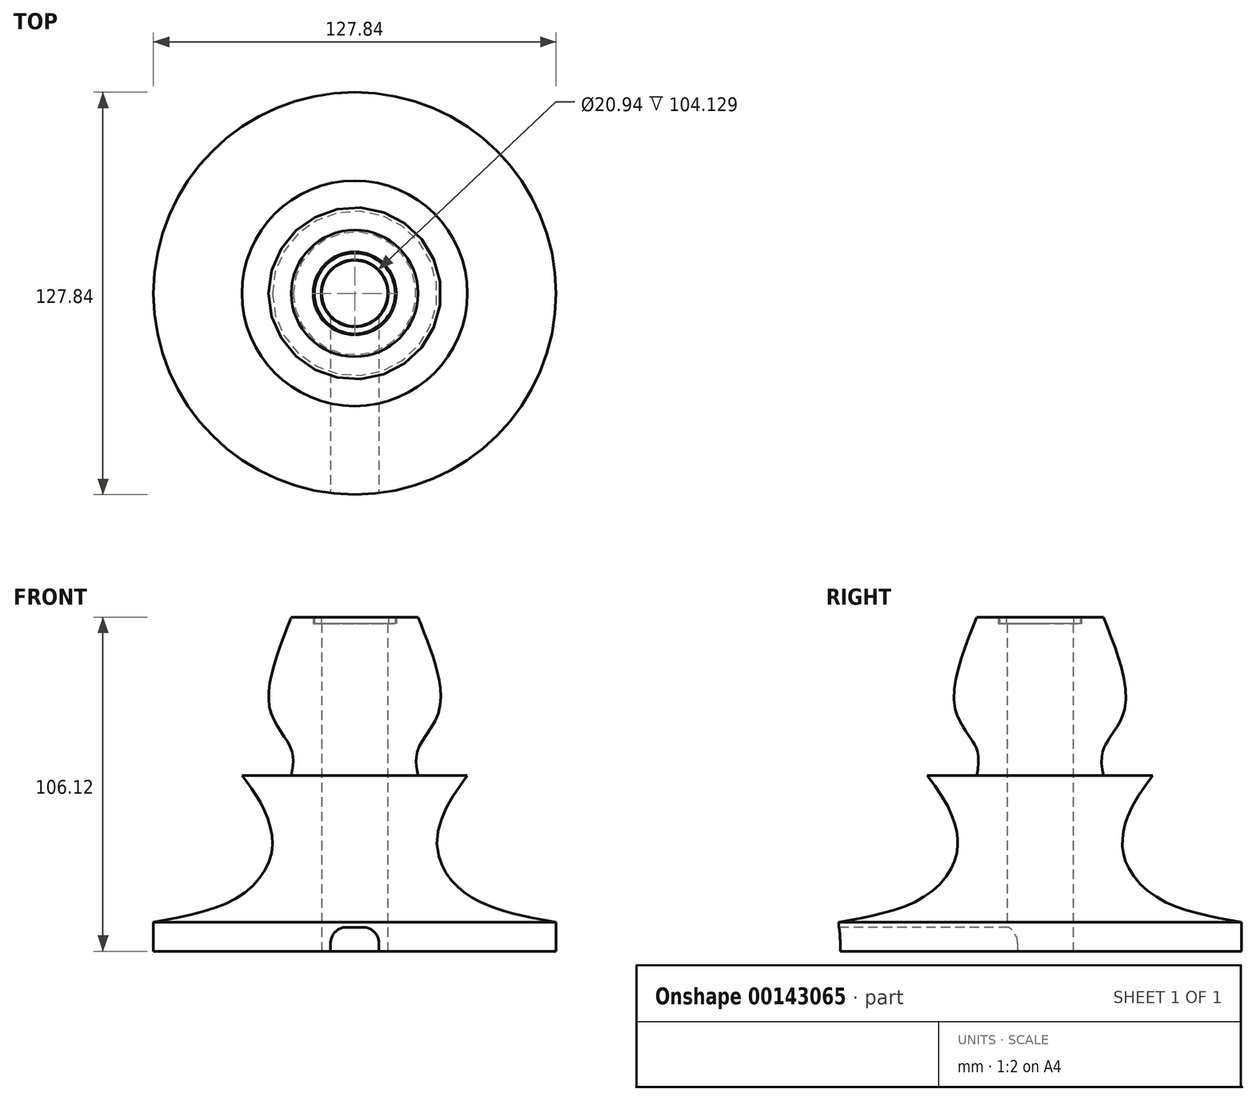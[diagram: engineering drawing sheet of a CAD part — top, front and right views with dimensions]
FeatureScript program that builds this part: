
annotation { "Feature Type Name" : "Feature", "Feature Type Description" : "" }
export const myFeature = defineFeature(function(context is Context, id is Id, definition is map)
    precondition{}
    {
        {
            var Q0;
            Q0=qCreatedBy(makeId("Front.planeOp"),FACE);
            var sketch = newSketch(context, id + "F0", { "sketchPlane" : qUnion([Q0])});
            skLineSegment(sketch, "E0", {"start": v(58.87, -65.2) * mm, "end": v(58.87, 68.15) * mm});
            skFitSpline(sketch, "E1", {"points": [v(-5.05, -65.2) * mm, v(21.76, -57.31) * mm, v(32.42, -43.38) * mm, v(29.96, -29.2) * mm, v(23.07, -18.67) * mm], "startDerivative": vector(93.9, 16.78) * mm, "endDerivative": vector(-35.35, 46.61) * mm});
            skLineSegment(sketch, "E2", {"start": v(23.07, -18.67) * mm, "end": v(38.74, -18.67) * mm});
            skFitSpline(sketch, "E3", {"points": [v(38.74, -18.67) * mm, v(38.74, -10.24) * mm, v(31.95, 2.53) * mm, v(38.74, 31.68) * mm], "startDerivative": vector(6.74, 35.22) * mm, "endDerivative": vector(28.6, 71.92) * mm});
            skLineSegment(sketch, "E4", {"start": v(38.74, 31.68) * mm, "end": v(42.98, 31.68) * mm});
            skLineSegment(sketch, "E5", {"start": v(42.98, 31.68) * mm, "end": v(45.68, 31.68) * mm});
            skLineSegment(sketch, "E6", {"start": v(45.68, 31.68) * mm, "end": v(45.68, 29.7) * mm});
            skLineSegment(sketch, "E7", {"start": v(-5.05, -65.2) * mm, "end": v(-5.05, -74.44) * mm});
            skLineSegment(sketch, "E8", {"start": v(-5.05, -74.44) * mm, "end": v(51.2, -74.44) * mm});
            skLineSegment(sketch, "E9", {"start": v(51.2, -74.44) * mm, "end": v(51.2, -65.2) * mm});
            skLineSegment(sketch, "E10", {"start": v(51.2, -65.2) * mm, "end": v(51.2, 29.7) * mm});
            skLineSegment(sketch, "E11", {"start": v(45.68, 29.7) * mm, "end": v(51.2, 29.7) * mm});
            skSolve(sketch);
        }
        {
            var Q0;
            Q0=makeQuery(id+"F0.imprint","IMPRINT",FACE,{"disambiguationData":[TD([[makeQuery(id+"F0.imprint","IMPRINT",EDGE,{"derivedFrom":sQuery(id+"F0.wireOp",EDGE,"E1")}),-1.0]])]});
            var Q1;
            Q1=sQuery(id+"F0.wireOp",EDGE,"E0");
            revolve(context, id + "F1", {"entities" : qUnion([Q0]), "axis" : qUnion([Q1]), "revolveType" : RevolveType.FULL});
        }
        {
            var Q0;
            Q0=makeQuery(id+"F1.opRevolve","SWEPT_FACE",FACE,{"disambiguationData":[OSD([sQuery(id+"F0.wireOp",EDGE,"E8")])]});
            var sketch = newSketch(context, id + "F2", { "sketchPlane" : qUnion([Q0])});
            skLineSegment(sketch, "E12", {"start": v(66.55, 0) * mm, "end": v(66.55, 63.46) * mm});
            skLineSegment(sketch, "E13", {"start": v(51.2, 0) * mm, "end": v(51.2, 63.46) * mm});
            skCircle(sketch, "E14", {"center": v(58.87, 0) * mm, "radius": 10.47 * mm});
            skSolve(sketch);
        }
        {
            var Q0;
            {var subQ0=sQuery(id+"F2.wireOp",EDGE,"E12");Q0=makeQuery(id+"F2.imprint","IMPRINT",FACE,{"disambiguationData":[TD([[makeQuery(id+"F2.imprint","IMPRINT",EDGE,{"derivedFrom":subQ0}),1.0]])]});}
            extrude(context, id + "F3", {"entities" : qUnion([Q0]), "operationType" : NewBodyOperationType.REMOVE, "oppositeDirection" : true, "depth" : 7.62 * mm});
        }
        {
            var Q0;
            Q0=makeQuery(id+"F3.boolean.opBoolean","COPY",EDGE,{"derivedFrom":makeQuery(id+"F3.opExtrude","CAP_EDGE",EDGE,{"disambiguationData":[OSD([sQuery(id+"F2.wireOp",EDGE,"E12")])],"isStart":false})});
            var Q1;
            Q1=makeQuery(id+"F3.boolean.opBoolean","COPY",EDGE,{"derivedFrom":makeQuery(id+"F3.opExtrude","CAP_EDGE",EDGE,{"disambiguationData":[OSD([sQuery(id+"F2.wireOp",EDGE,"E13")])],"isStart":false})});
            fillet(context, id + "F4", {"entities" : qUnion([Q0, Q1]), "radius" : 5.08 * mm, "tangentPropagation" : true, "allowEdgeOverflow" : false});
        }
        {
            var Q0;
            {var subQ0=sQuery(id+"F2.wireOp",EDGE,"E12");var subQ3=sQuery(id+"F2.wireOp",EDGE,"E14");var subQ4=makeQuery(id+"F2.imprint","INTERSECT",VERTEX,{"derivedFrom":[subQ0,subQ3]});Q0=makeQuery(id+"F2.imprint","IMPRINT",FACE,{"disambiguationData":[TD([[makeQuery(id+"F2.imprint","IMPRINT",EDGE,{"disambiguationData":[TD([[subQ4,1.0]])],"derivedFrom":subQ3}),1.0]])]});}
            var Q1;
            {var subQ0=sQuery(id+"F2.wireOp",EDGE,"E12");var subQ3=sQuery(id+"F2.wireOp",EDGE,"E14");var subQ4=makeQuery(id+"F2.imprint","INTERSECT",VERTEX,{"derivedFrom":[subQ0,subQ3]});Q1=makeQuery(id+"F2.imprint","IMPRINT",FACE,{"disambiguationData":[TD([[makeQuery(id+"F2.imprint","IMPRINT",EDGE,{"disambiguationData":[TD([[subQ4,-1.0]])],"derivedFrom":subQ3}),1.0]])]});}
            extrude(context, id + "F5", {"entities" : qUnion([Q0, Q1]), "operationType" : NewBodyOperationType.REMOVE, "oppositeDirection" : true, "depth" : 114.75 * mm});
        }
        {
            var Q0;
            Q0=makeQuery(id+"F1.opRevolve","SWEPT_FACE",FACE,{"disambiguationData":[OSD([sQuery(id+"F0.wireOp",EDGE,"E11")])]});
            var sketch = newSketch(context, id + "F6", { "sketchPlane" : qUnion([Q0])});
            skCircle(sketch, "E15", {"center": v(58.87, 0) * mm, "radius": 12.83 * mm});
            skCircle(sketch, "E16", {"center": v(58.87, 0) * mm, "radius": 10.69 * mm});
            skSolve(sketch);
        }
        {
            var Q0;
            Q0=makeQuery(id+"F6.imprint","IMPRINT",FACE,{"disambiguationData":[TD([[makeQuery(id+"F6.imprint","IMPRINT",EDGE,{"derivedFrom":sQuery(id+"F6.wireOp",EDGE,"E15")}),1.0]])]});
            extrude(context, id + "F7", {"entities" : qUnion([Q0]), "operationType" : NewBodyOperationType.ADD, "depth" : 1.91 * mm});
        }
    });
